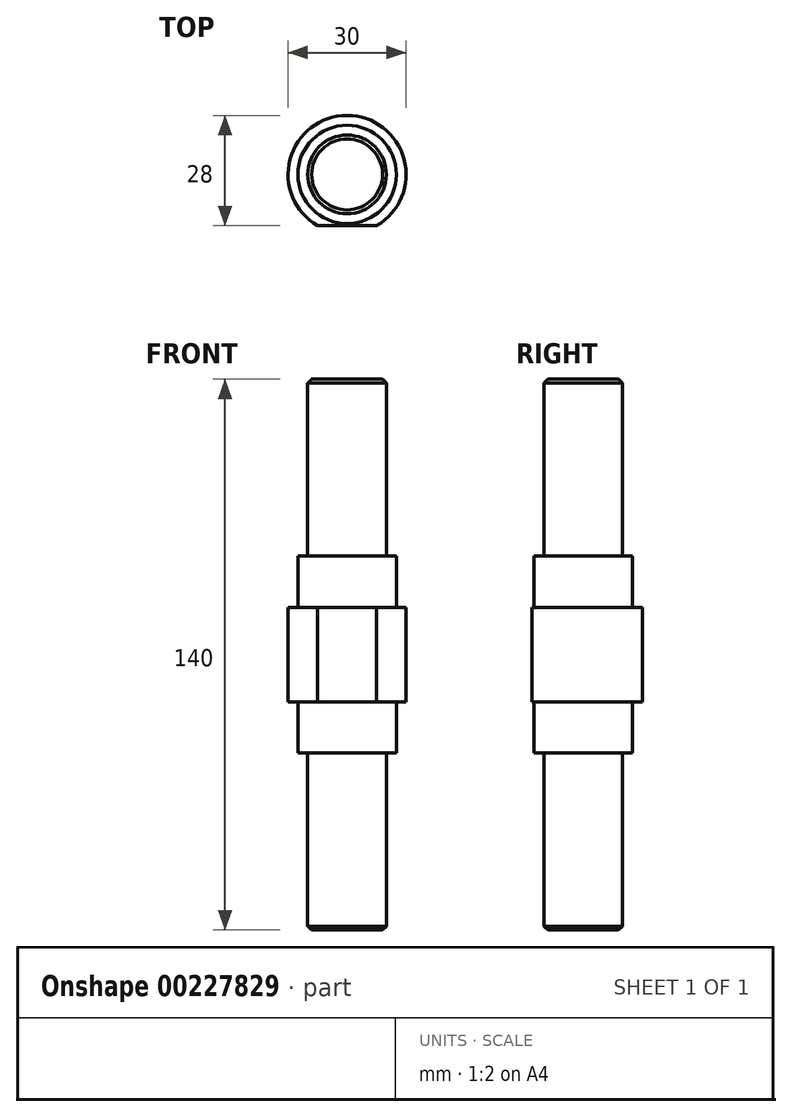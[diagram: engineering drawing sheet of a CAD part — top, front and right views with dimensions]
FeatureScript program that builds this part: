
annotation { "Feature Type Name" : "Feature", "Feature Type Description" : "" }
export const myFeature = defineFeature(function(context is Context, id is Id, definition is map)
    precondition{}
    {
        {
            var Q0;
            Q0=qCreatedBy(makeId("Front.planeOp"),FACE);
            var sketch = newSketch(context, id + "F0", { "sketchPlane" : qUnion([Q0])});
            skLineSegment(sketch, "E0", {"start": v(-15, 12) * mm, "end": v(-15, 0) * mm});
            skLineSegment(sketch, "E1", {"start": v(-10, 70) * mm, "end": v(0, 70) * mm});
            skLineSegment(sketch, "E2.MirrorCS", {"start": v(-15, 0) * mm, "end": v(-15, 12) * mm});
            skLineSegment(sketch, "E3", {"start": v(0, 70) * mm, "end": v(0, 0) * mm});
            skLineSegment(sketch, "E4", {"start": v(-15, 12) * mm, "end": v(-12.5, 12) * mm});
            skLineSegment(sketch, "E5", {"start": v(-12.5, 25) * mm, "end": v(-12.5, 12) * mm});
            skLineSegment(sketch, "E6", {"start": v(-12.5, 25) * mm, "end": v(-10, 25) * mm});
            skLineSegment(sketch, "E7", {"start": v(-10, 70) * mm, "end": v(-10, 25) * mm});
            skLineSegment(sketch, "E8", {"start": v(12.24, 0) * mm, "end": v(-26.8, 0) * mm, "construction": true});
            skLineSegment(sketch, "E9.MirrorCS", {"start": v(0, -70) * mm, "end": v(0, 0) * mm});
            skLineSegment(sketch, "E10.MirrorCS", {"start": v(-10, -70) * mm, "end": v(0, -70) * mm});
            skLineSegment(sketch, "E11.MirrorCS", {"start": v(-10, -70) * mm, "end": v(-10, -25) * mm});
            skLineSegment(sketch, "E12.MirrorCS", {"start": v(-12.5, -25) * mm, "end": v(-10, -25) * mm});
            skLineSegment(sketch, "E13.MirrorCS", {"start": v(-12.5, -25) * mm, "end": v(-12.5, -12) * mm});
            skLineSegment(sketch, "E14.MirrorCS", {"start": v(-15, -12) * mm, "end": v(-12.5, -12) * mm});
            skLineSegment(sketch, "E15.MirrorCS", {"start": v(-15, 0) * mm, "end": v(-15, -12) * mm});
            skSolve(sketch);
        }
        {
            var Q0;
            Q0 = qSketchRegion(id + "F0", true);
            var Q1;
            Q1=sQuery(id+"F0.wireOp",EDGE,"E3");
            revolve(context, id + "F1", {"entities" : qUnion([Q0]), "axis" : qUnion([Q1]), "revolveType" : RevolveType.FULL});
        }
        {
            var Q0;
            Q0=qCreatedBy(makeId("Top.planeOp"),FACE);
            var sketch = newSketch(context, id + "F2", { "sketchPlane" : qUnion([Q0])});
            skCircle(sketch, "E16.0", {"center": v(0, 0) * mm, "radius": 12.5 * mm, "construction": true});
            skLineSegment(sketch, "E17", {"start": v(-18, -12.5) * mm, "end": v(24.59, -12.5) * mm, "construction": true});
            skLineSegment(sketch, "E18", {"start": v(-15, -13) * mm, "end": v(0, -13) * mm});
            skLineSegment(sketch, "E19", {"start": v(-15, -17) * mm, "end": v(0, -17) * mm});
            skLineSegment(sketch, "E20.trimOffspring", {"start": v(-15, -13) * mm, "end": v(-15, -17) * mm});
            skLineSegment(sketch, "E21.MirrorCS", {"start": v(15, -13) * mm, "end": v(0, -13) * mm});
            skLineSegment(sketch, "E22.MirrorCS", {"start": v(15, -13) * mm, "end": v(15, -17) * mm});
            skLineSegment(sketch, "E23.MirrorCS", {"start": v(15, -17) * mm, "end": v(0, -17) * mm});
            skSolve(sketch);
        }
        {
            var Q0;
            Q0 = qSketchRegion(id + "F2", true);
            extrude(context, id + "F3", {"entities" : qUnion([Q0]), "operationType" : NewBodyOperationType.REMOVE, "depth" : 25 * mm, "hasSecondDirection" : true, "secondDirectionOppositeDirection" : true, "secondDirectionDepth" : 25 * mm});
        }
        {
            var Q0;
            Q0=makeQuery(id+"F1.opRevolve","SWEPT_EDGE",EDGE,{"disambiguationData":[OSD([sQuery(id+"F0.wireOp",EDGE,"E1"),sQuery(id+"F0.wireOp",EDGE,"E7")])]});
            var Q1;
            Q1=makeQuery(id+"F1.opRevolve","SWEPT_EDGE",EDGE,{"disambiguationData":[OSD([sQuery(id+"F0.wireOp",EDGE,"E10.MirrorCS"),sQuery(id+"F0.wireOp",EDGE,"E11.MirrorCS")])]});
            chamfer(context, id + "F4", {"entities" : qUnion([Q0, Q1]), "width" : 1 * mm, "tangentPropagation" : true});
        }
    });
